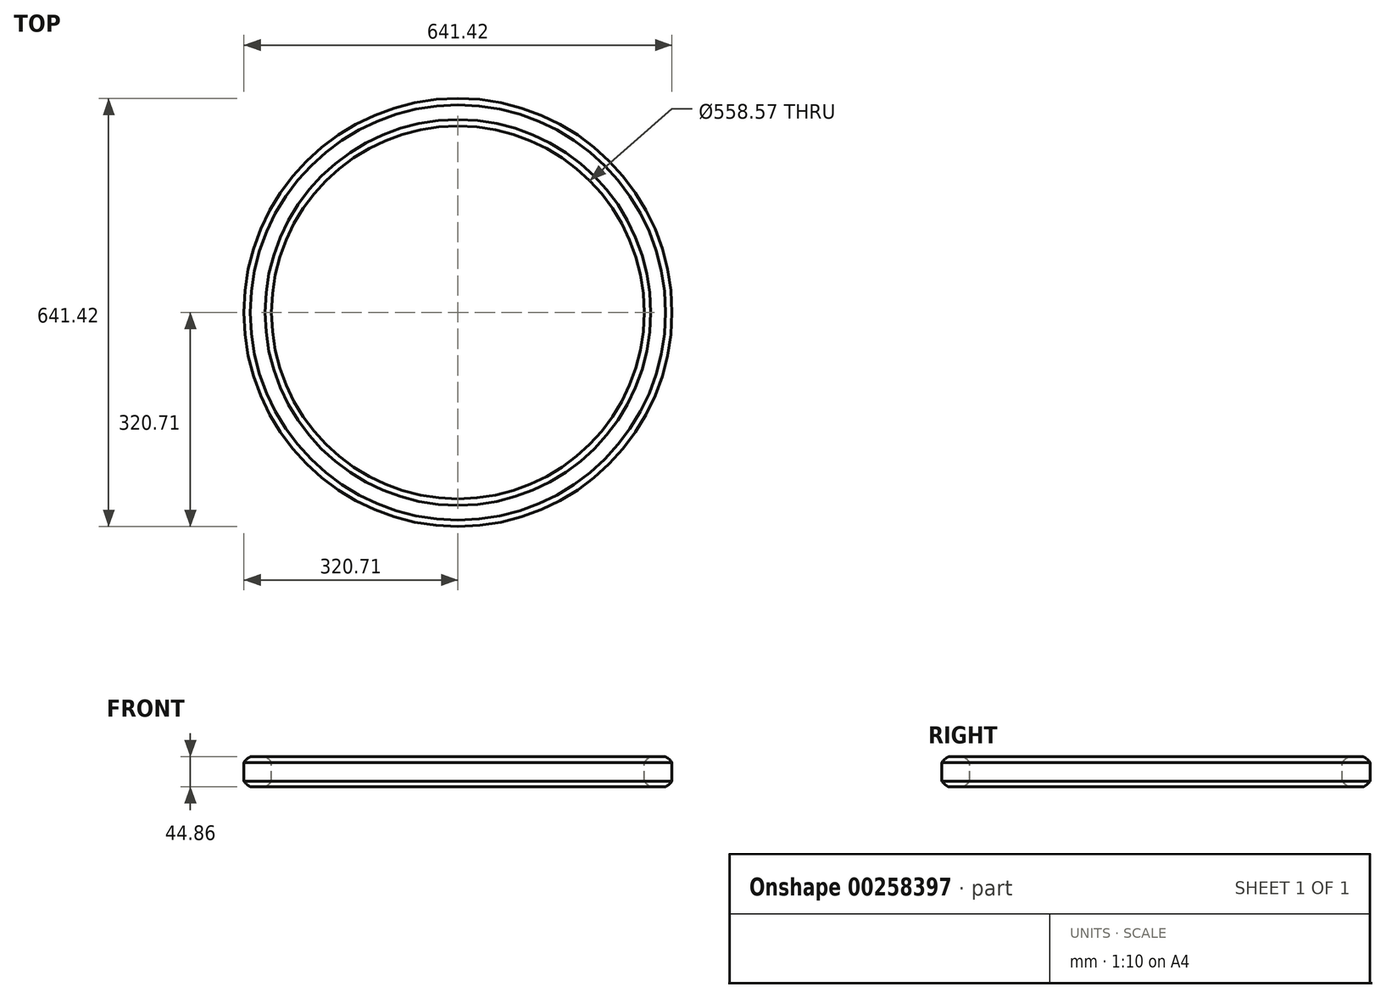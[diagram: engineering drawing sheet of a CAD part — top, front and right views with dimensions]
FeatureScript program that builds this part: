
annotation { "Feature Type Name" : "Feature", "Feature Type Description" : "" }
export const myFeature = defineFeature(function(context is Context, id is Id, definition is map)
    precondition{}
    {
        {
            var Q0;
            Q0=qCreatedBy(makeId("Front.planeOp"),FACE);
            var sketch = newSketch(context, id + "F0", { "sketchPlane" : qUnion([Q0])});
            skCircle(sketch, "E0", {"center": v(300, 0) * mm, "radius": 25 * mm});
            skLineSegment(sketch, "E1", {"start": v(0, 73.43) * mm, "end": v(0, -79.94) * mm, "construction": true});
            skLineSegment(sketch, "E2.bottom", {"start": v(320.71, -22.43) * mm, "end": v(279.29, -22.43) * mm});
            skLineSegment(sketch, "E2.top", {"start": v(320.71, 22.43) * mm, "end": v(279.29, 22.43) * mm});
            skLineSegment(sketch, "E2.left", {"start": v(320.71, -22.43) * mm, "end": v(320.71, 22.43) * mm});
            skLineSegment(sketch, "E2.right", {"start": v(279.29, -22.43) * mm, "end": v(279.29, 22.43) * mm});
            skLineSegment(sketch, "E3", {"start": v(0, 0) * mm, "end": v(300, 0) * mm, "construction": true});
            skSolve(sketch);
        }
        {
            var Q0;
            Q0=makeQuery(id+"F0.imprint","IMPRINT",FACE,{"disambiguationData":[TD([[makeQuery(id+"F0.imprint","IMPRINT",EDGE,{"derivedFrom":sQuery(id+"F0.wireOp",EDGE,"E0")}),1.0]])]});
            var Q1;
            Q1=sQuery(id+"F0.wireOp",EDGE,"E0");
            var Q2;
            Q2=sQuery(id+"F0.wireOp",EDGE,"E2.top");
            var Q3;
            Q3=sQuery(id+"F0.wireOp",EDGE,"E1");
            revolve(context, id + "F1", {"entities" : qUnion([Q0]), "surfaceEntities" : qUnion([Q1, Q2]), "axis" : qUnion([Q3]), "revolveType" : RevolveType.FULL});
        }
    });
